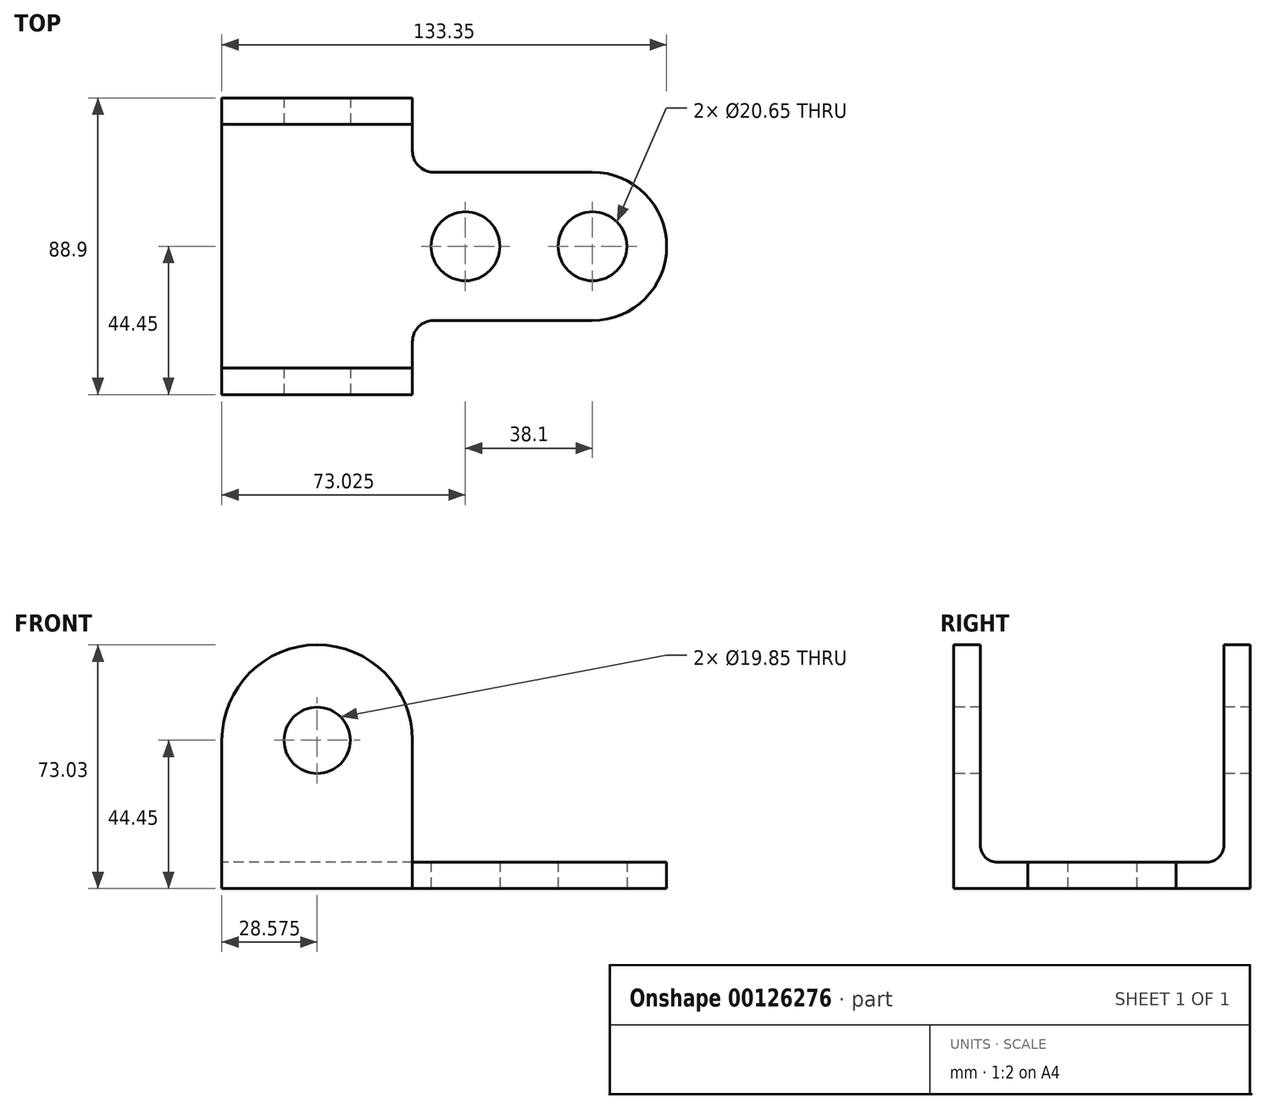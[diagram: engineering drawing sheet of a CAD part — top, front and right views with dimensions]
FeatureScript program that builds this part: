
annotation { "Feature Type Name" : "Feature", "Feature Type Description" : "" }
export const myFeature = defineFeature(function(context is Context, id is Id, definition is map)
    precondition{}
    {
        {
            var Q0;
            Q0=qCreatedBy(makeId("Top.planeOp"),FACE);
            var sketch = newSketch(context, id + "F0", { "sketchPlane" : qUnion([Q0])});
            skLineSegment(sketch, "E0", {"start": v(0, 0) * mm, "end": v(0, 88.9) * mm});
            skLineSegment(sketch, "E1", {"start": v(0, 88.9) * mm, "end": v(57.15, 88.9) * mm});
            skLineSegment(sketch, "E2", {"start": v(57.15, 88.9) * mm, "end": v(57.15, 73.03) * mm});
            skArc(sketch, "E3", {"start": v(57.15, 73.03) * mm, "mid": v(59, 68.53) * mm, "end": v(63.5, 66.68) * mm});
            skLineSegment(sketch, "E4", {"start": v(63.5, 66.68) * mm, "end": v(111.12, 66.68) * mm});
            skArc(sketch, "E5", {"start": v(111.12, 22.23) * mm, "mid": v(133.35, 44.45) * mm, "end": v(111.12, 66.68) * mm});
            skLineSegment(sketch, "E6", {"start": v(111.12, 22.23) * mm, "end": v(63.5, 22.23) * mm});
            skArc(sketch, "E7", {"start": v(63.5, 22.23) * mm, "mid": v(59, 20.37) * mm, "end": v(57.15, 15.88) * mm});
            skLineSegment(sketch, "E8", {"start": v(57.15, 15.88) * mm, "end": v(57.15, 0) * mm});
            skLineSegment(sketch, "E9", {"start": v(0, 0) * mm, "end": v(57.15, 0) * mm});
            skCircle(sketch, "E10", {"center": v(111.12, 44.45) * mm, "radius": 10.33 * mm});
            skCircle(sketch, "E11", {"center": v(73.03, 44.45) * mm, "radius": 10.33 * mm});
            skLineSegment(sketch, "E12", {"start": v(0, 7.94) * mm, "end": v(57.15, 7.94) * mm});
            skLineSegment(sketch, "E13", {"start": v(0, 80.96) * mm, "end": v(57.15, 80.96) * mm});
            skLineSegment(sketch, "E14", {"start": v(28.58, 7.94) * mm, "end": v(28.58, 0) * mm, "construction": true});
            skSolve(sketch);
        }
        {
            var Q0;
            Q0 = qSketchRegion(id + "F0", true);
            extrude(context, id + "F1", {"entities" : qUnion([Q0]), "depth" : 7.94 * mm});
        }
        {
            var Q0;
            {var subQ0=sQuery(id+"F0.wireOp",EDGE,"E9");Q0=makeQuery(id+"F0.imprint","IMPRINT",FACE,{"disambiguationData":[TD([[makeQuery(id+"F0.imprint","IMPRINT",EDGE,{"derivedFrom":subQ0}),1.0]])]});}
            extrude(context, id + "F2", {"entities" : qUnion([Q0]), "operationType" : NewBodyOperationType.ADD, "depth" : 44.45 * mm});
        }
        {
            var Q0;
            {var subQ0=sQuery(id+"F0.wireOp",EDGE,"E1");Q0=makeQuery(id+"F0.imprint","IMPRINT",FACE,{"disambiguationData":[TD([[makeQuery(id+"F0.imprint","IMPRINT",EDGE,{"derivedFrom":subQ0}),-1.0]])]});}
            extrude(context, id + "F3", {"entities" : qUnion([Q0]), "operationType" : NewBodyOperationType.ADD, "depth" : 44.45 * mm});
        }
        {
            var Q0;
            Q0=makeQuery(id+"F2.opExtrude","CAP_FACE",FACE,{"disambiguationData":[OSD([sQuery(id+"F0.wireOp",EDGE,"E0"),sQuery(id+"F0.wireOp",EDGE,"E8"),sQuery(id+"F0.wireOp",EDGE,"E9"),sQuery(id+"F0.wireOp",EDGE,"E12")])],"isStart":false});
            var sketch = newSketch(context, id + "F4", { "sketchPlane" : qUnion([Q0])});
            skLineSegment(sketch, "E15", {"start": v(0, 0) * mm, "end": v(28.57, 0) * mm});
            skLineSegment(sketch, "E16", {"start": v(28.58, 0) * mm, "end": v(28.58, 7.94) * mm});
            skLineSegment(sketch, "E17", {"start": v(28.58, 7.94) * mm, "end": v(0, 7.94) * mm});
            skLineSegment(sketch, "E18", {"start": v(0, 7.94) * mm, "end": v(0, 0) * mm});
            skSolve(sketch);
        }
        {
            var Q0;
            Q0=makeQuery(id+"F4.imprint","IMPRINT",FACE,{"disambiguationData":[TD([[makeQuery(id+"F4.imprint","IMPRINT",EDGE,{"derivedFrom":sQuery(id+"F4.wireOp",EDGE,"E15")}),1.0]])]});
            var Q1;
            Q1=sQuery(id+"F4.wireOp",EDGE,"E16");
            revolve(context, id + "F5", {"operationType" : NewBodyOperationType.ADD, "entities" : qUnion([Q0]), "axis" : qUnion([Q1]), "revolveType" : RevolveType.FULL});
        }
        {
            var Q0;
            Q0=makeQuery(id+"F3.opExtrude","CAP_FACE",FACE,{"disambiguationData":[OSD([sQuery(id+"F0.wireOp",EDGE,"E0"),sQuery(id+"F0.wireOp",EDGE,"E1"),sQuery(id+"F0.wireOp",EDGE,"E2"),sQuery(id+"F0.wireOp",EDGE,"E13")])],"isStart":false});
            var sketch = newSketch(context, id + "F6", { "sketchPlane" : qUnion([Q0])});
            skLineSegment(sketch, "E19", {"start": v(0, 80.96) * mm, "end": v(28.58, 80.96) * mm});
            skLineSegment(sketch, "E20", {"start": v(28.58, 80.96) * mm, "end": v(28.58, 88.9) * mm});
            skLineSegment(sketch, "E21", {"start": v(28.58, 88.9) * mm, "end": v(0, 88.9) * mm});
            skLineSegment(sketch, "E22", {"start": v(0, 88.9) * mm, "end": v(0, 80.96) * mm});
            skSolve(sketch);
        }
        {
            var Q0;
            Q0 = qSketchRegion(id + "F6", true);
            var Q1;
            Q1=sQuery(id+"F6.wireOp",EDGE,"E20");
            revolve(context, id + "F7", {"operationType" : NewBodyOperationType.ADD, "entities" : qUnion([Q0]), "axis" : qUnion([Q1]), "revolveType" : RevolveType.FULL});
        }
        {
            var Q0;
            {var subQ0=sQuery(id+"F0.wireOp",EDGE,"E9");Q0=makeQuery(id+"F5.boolean.opBoolean","MERGE",FACE,{"derivedFrom":[makeQuery(id+"F2.boolean.opBoolean","MERGE",FACE,{"derivedFrom":[makeQuery(id+"F1.opExtrude","SWEPT_FACE",FACE,{"disambiguationData":[OSD([subQ0])]}),makeQuery(id+"F2.opExtrude","SWEPT_FACE",FACE,{"disambiguationData":[OSD([subQ0])]})]}),makeQuery(id+"F5.opRevolve","SWEPT_FACE",FACE,{"disambiguationData":[OSD([sQuery(id+"F4.wireOp",EDGE,"E15")])]})]});}
            var sketch = newSketch(context, id + "F8", { "sketchPlane" : qUnion([Q0])});
            skCircle(sketch, "E23", {"center": v(28.57, 44.45) * mm, "radius": 9.92 * mm});
            skSolve(sketch);
        }
        {
            var Q0;
            Q0 = qSketchRegion(id + "F8", true);
            extrude(context, id + "F9", {"entities" : qUnion([Q0]), "operationType" : NewBodyOperationType.REMOVE, "endBound" : BoundingType.THROUGH_ALL, "oppositeDirection" : true, "depth" : 25.4 * mm});
        }
        {
            var Q0;
            Q0=makeQuery(id+"F3.boolean.opBoolean","INTERSECT",EDGE,{"derivedFrom":[makeQuery(id+"F1.opExtrude","CAP_FACE",FACE,{"disambiguationData":[OSD([sQuery(id+"F0.wireOp",EDGE,"E0"),sQuery(id+"F0.wireOp",EDGE,"E1"),sQuery(id+"F0.wireOp",EDGE,"E2"),sQuery(id+"F0.wireOp",EDGE,"E3"),sQuery(id+"F0.wireOp",EDGE,"E4"),sQuery(id+"F0.wireOp",EDGE,"E5"),sQuery(id+"F0.wireOp",EDGE,"E6"),sQuery(id+"F0.wireOp",EDGE,"E7"),sQuery(id+"F0.wireOp",EDGE,"E8"),sQuery(id+"F0.wireOp",EDGE,"E9"),sQuery(id+"F0.wireOp",EDGE,"E10"),sQuery(id+"F0.wireOp",EDGE,"E11")])],"isStart":false}),makeQuery(id+"F3.opExtrude","SWEPT_FACE",FACE,{"disambiguationData":[OSD([sQuery(id+"F0.wireOp",EDGE,"E13")])]})]});
            var Q1;
            Q1=makeQuery(id+"F2.boolean.opBoolean","INTERSECT",EDGE,{"derivedFrom":[makeQuery(id+"F1.opExtrude","CAP_FACE",FACE,{"disambiguationData":[OSD([sQuery(id+"F0.wireOp",EDGE,"E0"),sQuery(id+"F0.wireOp",EDGE,"E1"),sQuery(id+"F0.wireOp",EDGE,"E2"),sQuery(id+"F0.wireOp",EDGE,"E3"),sQuery(id+"F0.wireOp",EDGE,"E4"),sQuery(id+"F0.wireOp",EDGE,"E5"),sQuery(id+"F0.wireOp",EDGE,"E6"),sQuery(id+"F0.wireOp",EDGE,"E7"),sQuery(id+"F0.wireOp",EDGE,"E8"),sQuery(id+"F0.wireOp",EDGE,"E9"),sQuery(id+"F0.wireOp",EDGE,"E10"),sQuery(id+"F0.wireOp",EDGE,"E11")])],"isStart":false}),makeQuery(id+"F2.opExtrude","SWEPT_FACE",FACE,{"disambiguationData":[OSD([sQuery(id+"F0.wireOp",EDGE,"E12")])]})]});
            fillet(context, id + "F10", {"entities" : qUnion([Q0, Q1]), "radius" : 5.08 * mm, "tangentPropagation" : true, "allowEdgeOverflow" : false});
        }
    });
